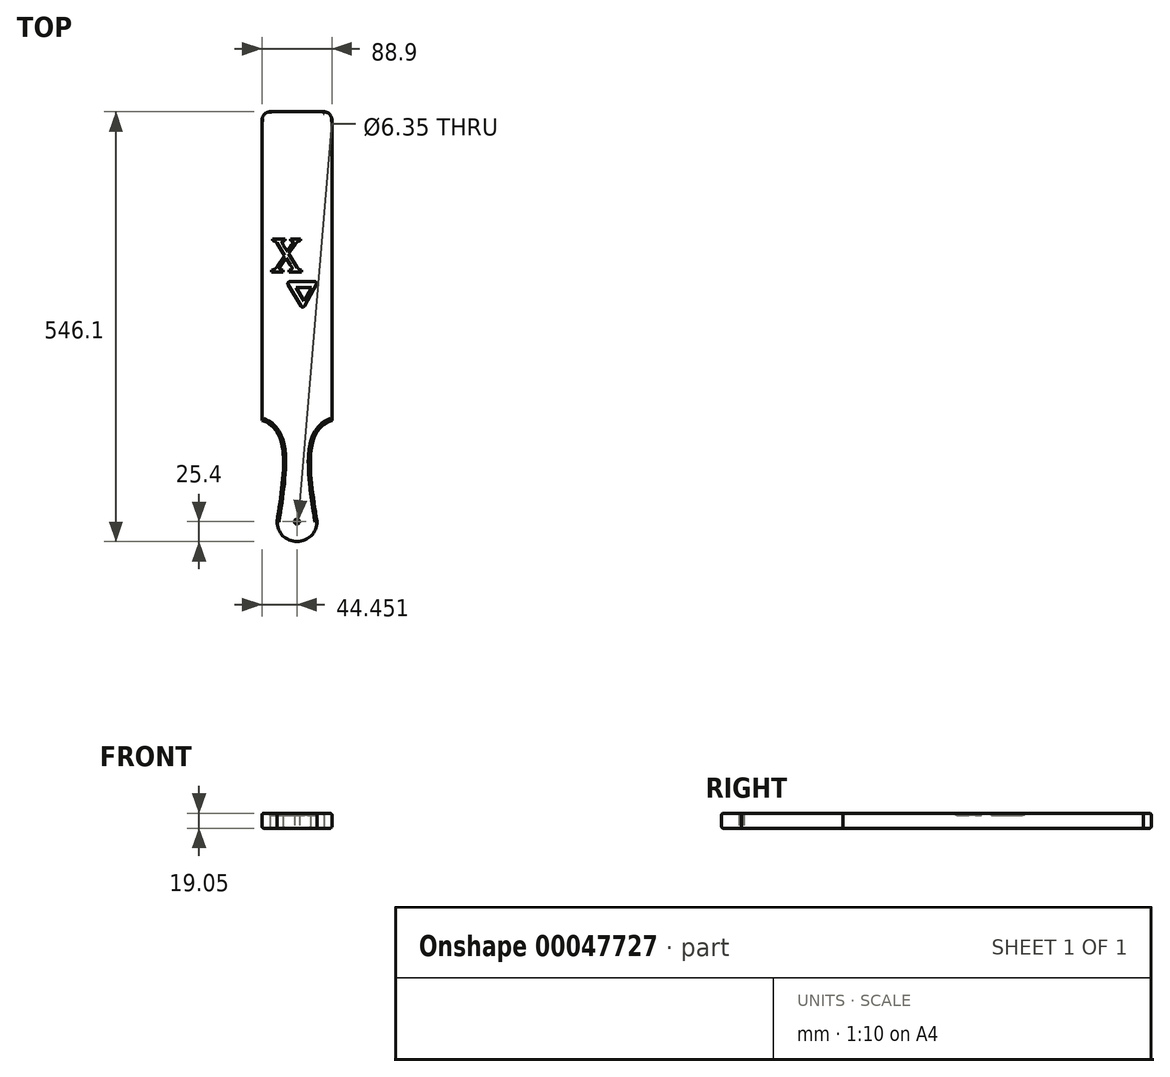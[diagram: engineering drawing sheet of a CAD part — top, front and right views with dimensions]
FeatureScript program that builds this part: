
annotation { "Feature Type Name" : "Feature", "Feature Type Description" : "" }
export const myFeature = defineFeature(function(context is Context, id is Id, definition is map)
    precondition{}
    {
        {
            var Q0;
            Q0=qCreatedBy(makeId("Top.planeOp"),FACE);
            var sketch = newSketch(context, id + "F0", { "sketchPlane" : qUnion([Q0])});
            skLineSegment(sketch, "E0.bottom", {"start": v(-63.25, -115.13) * mm, "end": v(25.65, -115.13) * mm});
            skLineSegment(sketch, "E0.top", {"start": v(-63.25, 443.67) * mm, "end": v(25.65, 443.67) * mm});
            skLineSegment(sketch, "E0.left", {"start": v(-63.25, -115.13) * mm, "end": v(-63.25, 443.67) * mm});
            skLineSegment(sketch, "E0.right", {"start": v(25.65, -115.13) * mm, "end": v(25.65, 443.67) * mm});
            skCircle(sketch, "E1", {"center": v(-18.8, -77.03) * mm, "radius": 3.18 * mm});
            skArc(sketch, "E2", {"start": v(-44.2, -77.03) * mm, "mid": v(-18.8, -102.43) * mm, "end": v(6.6, -77.03) * mm});
            skLineSegment(sketch, "E3", {"start": v(-18.8, -102.43) * mm, "end": v(-18.8, 37.27) * mm, "construction": true});
            skFitSpline(sketch, "E4", {"points": [v(6.6, -77.03) * mm, v(6.6, 37.19) * mm, v(25.65, 51.65) * mm, v(25.65, 50.95) * mm], "startDerivative": vector(-33.54, 212.28) * mm, "endDerivative": vector(-5.78, -17.03) * mm});
            skFitSpline(sketch, "E5.MirrorCS", {"points": [v(-44.2, -77.03) * mm, v(-44.2, 37.19) * mm, v(-63.25, 51.65) * mm, v(-63.25, 50.95) * mm], "startDerivative": vector(33.54, 212.28) * mm, "endDerivative": vector(5.78, -17.03) * mm});
            skArc(sketch, "E6", {"start": v(-63.25, 433.27) * mm, "mid": v(-60.17, 440.53) * mm, "end": v(-52.93, 443.67) * mm});
            skLineSegment(sketch, "E7", {"start": v(-63.25, 443.67) * mm, "end": v(-18.8, 443.67) * mm, "construction": true});
            skLineSegment(sketch, "E8", {"start": v(-18.8, 443.67) * mm, "end": v(-18.8, 406.08) * mm, "construction": true});
            skArc(sketch, "E9.MirrorCS", {"start": v(25.65, 433.27) * mm, "mid": v(22.57, 440.53) * mm, "end": v(15.33, 443.67) * mm});
            skSolve(sketch);
        }
        {
            var Q0;
            Q0=makeQuery(id+"F0.imprint","IMPRINT",FACE,{"disambiguationData":[TD([[makeQuery(id+"F0.imprint","IMPRINT",EDGE,{"derivedFrom":sQuery(id+"F0.wireOp",EDGE,"E1")}),-1.0]])]});
            extrude(context, id + "F1", {"entities" : qUnion([Q0]), "depth" : 19.05 * mm});
        }
        {
            var Q0;
            Q0=makeQuery(id+"F1.opExtrude","CAP_EDGE",EDGE,{"disambiguationData":[OSD([sQuery(id+"F0.wireOp",EDGE,"E0.right")])],"isStart":false});
            var Q1;
            Q1=makeQuery(id+"F1.opExtrude","CAP_EDGE",EDGE,{"disambiguationData":[OSD([sQuery(id+"F0.wireOp",EDGE,"E4")])],"isStart":false});
            var Q2;
            Q2=makeQuery(id+"F1.opExtrude","CAP_EDGE",EDGE,{"disambiguationData":[OSD([sQuery(id+"F0.wireOp",EDGE,"E2")])],"isStart":false});
            var Q3;
            Q3=makeQuery(id+"F1.opExtrude","CAP_EDGE",EDGE,{"disambiguationData":[OSD([sQuery(id+"F0.wireOp",EDGE,"E5.MirrorCS")])],"isStart":false});
            var Q4;
            Q4=makeQuery(id+"F1.opExtrude","CAP_EDGE",EDGE,{"disambiguationData":[OSD([sQuery(id+"F0.wireOp",EDGE,"E0.left")])],"isStart":false});
            var Q5;
            Q5=makeQuery(id+"F1.opExtrude","CAP_EDGE",EDGE,{"disambiguationData":[OSD([sQuery(id+"F0.wireOp",EDGE,"E6")])],"isStart":false});
            var Q6;
            Q6=makeQuery(id+"F1.opExtrude","CAP_EDGE",EDGE,{"disambiguationData":[OSD([sQuery(id+"F0.wireOp",EDGE,"E9.MirrorCS")])],"isStart":false});
            var Q7;
            Q7=makeQuery(id+"F1.opExtrude","CAP_EDGE",EDGE,{"disambiguationData":[OSD([sQuery(id+"F0.wireOp",EDGE,"E0.top")])],"isStart":false});
            fillet(context, id + "F2", {"entities" : qUnion([Q0, Q1, Q2, Q3, Q4, Q5, Q6, Q7]), "radius" : 2.54 * mm, "tangentPropagation" : true, "allowEdgeOverflow" : false});
        }
        {
            var Q0;
            Q0=makeQuery(id+"F1.opExtrude","CAP_EDGE",EDGE,{"disambiguationData":[OSD([sQuery(id+"F0.wireOp",EDGE,"E4")])],"isStart":true});
            var Q1;
            Q1=makeQuery(id+"F1.opExtrude","CAP_EDGE",EDGE,{"disambiguationData":[OSD([sQuery(id+"F0.wireOp",EDGE,"E2")])],"isStart":true});
            var Q2;
            Q2=makeQuery(id+"F1.opExtrude","CAP_EDGE",EDGE,{"disambiguationData":[OSD([sQuery(id+"F0.wireOp",EDGE,"E5.MirrorCS")])],"isStart":true});
            var Q3;
            Q3=makeQuery(id+"F1.opExtrude","CAP_EDGE",EDGE,{"disambiguationData":[OSD([sQuery(id+"F0.wireOp",EDGE,"E0.left")])],"isStart":true});
            var Q4;
            Q4=makeQuery(id+"F1.opExtrude","CAP_EDGE",EDGE,{"disambiguationData":[OSD([sQuery(id+"F0.wireOp",EDGE,"E0.right")])],"isStart":true});
            var Q5;
            Q5=makeQuery(id+"F1.opExtrude","CAP_EDGE",EDGE,{"disambiguationData":[OSD([sQuery(id+"F0.wireOp",EDGE,"E9.MirrorCS")])],"isStart":true});
            var Q6;
            Q6=makeQuery(id+"F1.opExtrude","CAP_EDGE",EDGE,{"disambiguationData":[OSD([sQuery(id+"F0.wireOp",EDGE,"E0.top")])],"isStart":true});
            var Q7;
            Q7=makeQuery(id+"F1.opExtrude","CAP_EDGE",EDGE,{"disambiguationData":[OSD([sQuery(id+"F0.wireOp",EDGE,"E6")])],"isStart":true});
            fillet(context, id + "F3", {"entities" : qUnion([Q0, Q1, Q2, Q3, Q4, Q5, Q6, Q7]), "radius" : 2.54 * mm, "tangentPropagation" : true, "allowEdgeOverflow" : false});
        }
        {
            var Q0;
            Q0=makeQuery(id+"F1.opExtrude","CAP_EDGE",EDGE,{"disambiguationData":[OSD([sQuery(id+"F0.wireOp",EDGE,"E1")])],"isStart":false});
            fillet(context, id + "F4", {"entities" : qUnion([Q0]), "radius" : 0.5 * mm, "tangentPropagation" : true, "allowEdgeOverflow" : false});
        }
        {
            var Q0;
            Q0=makeQuery(id+"F1.opExtrude","CAP_EDGE",EDGE,{"disambiguationData":[OSD([sQuery(id+"F0.wireOp",EDGE,"E1")])],"isStart":true});
            fillet(context, id + "F5", {"entities" : qUnion([Q0]), "radius" : 0.5 * mm, "tangentPropagation" : true, "allowEdgeOverflow" : false});
        }
        {
            var Q0;
            Q0=makeQuery(id+"F1.opExtrude","CAP_FACE",FACE,{"disambiguationData":[OSD([sQuery(id+"F0.wireOp",EDGE,"E0.top"),sQuery(id+"F0.wireOp",EDGE,"E0.left"),sQuery(id+"F0.wireOp",EDGE,"E0.right"),sQuery(id+"F0.wireOp",EDGE,"E1"),sQuery(id+"F0.wireOp",EDGE,"E2"),sQuery(id+"F0.wireOp",EDGE,"E4"),sQuery(id+"F0.wireOp",EDGE,"E5.MirrorCS"),sQuery(id+"F0.wireOp",EDGE,"E6"),sQuery(id+"F0.wireOp",EDGE,"E9.MirrorCS")])],"isStart":false});
            cPlane(context, id + "F6", {"entities" : qUnion([Q0]), "cplaneType" : CPlaneType.OFFSET, "offset" : 0 * mm, "width" : 152.4 * mm, "height" : 152.4 * mm});
        }
        {
            var Q0;
            Q0=qCreatedBy(id+"F6.planeOp",FACE);
            var sketch = newSketch(context, id + "F7", { "sketchPlane" : qUnion([Q0])});
            skText(sketch, "E10", { "text": "X", "fontName": "NotoSerif-Regular.ttf"});
            skLineSegment(sketch, "E11", {"start": v(0, 220.64) * mm, "end": v(-20.16, 220.64) * mm});
            skLineSegment(sketch, "E12", {"start": v(0, 220.64) * mm, "end": v(-10.08, 203.18) * mm});
            skLineSegment(sketch, "E13", {"start": v(-10.08, 203.18) * mm, "end": v(-20.16, 220.64) * mm});
            skLineSegment(sketch, "E14", {"start": v(0, 227.79) * mm, "end": v(-28.06, 227.79) * mm});
            skLineSegment(sketch, "E15", {"start": v(4.43, 221.68) * mm, "end": v(-9.29, 196.83) * mm});
            skLineSegment(sketch, "E16", {"start": v(-13.69, 196.83) * mm, "end": v(-30.1, 223.91) * mm});
            skLineSegment(sketch, "E17", {"start": v(0, 227.79) * mm, "end": v(3.92, 227.79) * mm});
            skLineSegment(sketch, "E18", {"start": v(4.43, 221.68) * mm, "end": v(6.08, 224.67) * mm});
            skArc(sketch, "E19", {"start": v(-9.29, 196.83) * mm, "mid": v(-11.49, 195.53) * mm, "end": v(-13.69, 196.83) * mm});
            skArc(sketch, "E20", {"start": v(-30.1, 223.91) * mm, "mid": v(-30.17, 226.42) * mm, "end": v(-28.06, 227.79) * mm});
            skArc(sketch, "E21", {"start": v(3.92, 227.79) * mm, "mid": v(5.82, 226.8) * mm, "end": v(6.08, 224.67) * mm});
            const initialGuessF7  = {"E10": [-0.05118, 0.24032, 1, 0, 0.04225]};
            skSetInitialGuess(sketch, initialGuessF7);
            skSolve(sketch);
        }
        {
            var Q0;
            Q0=makeQuery(id+"F7.imprint","IMPRINT",FACE,{"disambiguationData":[TD([[makeQuery(id+"F7.imprint","IMPRINT",EDGE,{"derivedFrom":sQuery(id+"F7.wireOp",EDGE,"E11")}),-1.0]])]});
            var Q1;
            Q1=makeQuery(id+"F7.imprint","IMPRINT",FACE,{"disambiguationData":[TD([[makeQuery(id+"F7.imprint","IMPRINT",EDGE,{"derivedFrom":sQuery(id+"F7.wireOp",EDGE,"E10.sketch_text.stroke-0")}),-1.0]])]});
            extrude(context, id + "F8", {"entities" : qUnion([Q0, Q1]), "operationType" : NewBodyOperationType.REMOVE, "oppositeDirection" : true, "depth" : 2.54 * mm});
        }
    });
